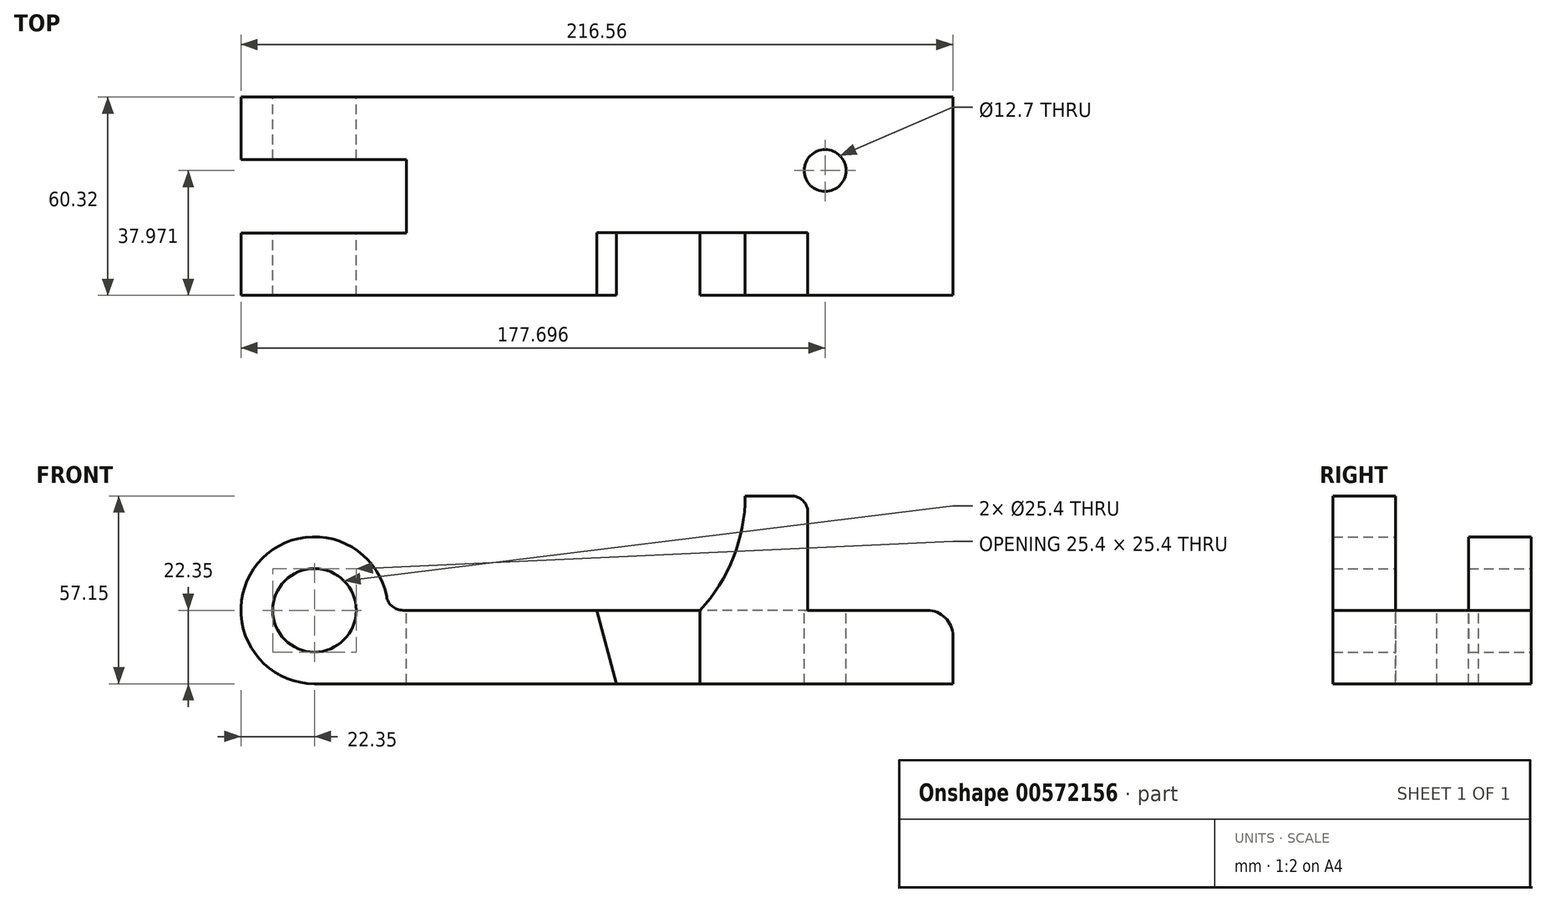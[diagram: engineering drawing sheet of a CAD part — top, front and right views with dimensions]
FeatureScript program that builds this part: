
annotation { "Feature Type Name" : "Feature", "Feature Type Description" : "" }
export const myFeature = defineFeature(function(context is Context, id is Id, definition is map)
    precondition{}
    {
        {
            var Q0;
            Q0=qCreatedBy(makeId("Front.planeOp"),FACE);
            var sketch = newSketch(context, id + "F0", { "sketchPlane" : qUnion([Q0])});
            skCircle(sketch, "E0", {"center": v(0, 0) * mm, "radius": 12.7 * mm});
            skCircle(sketch, "E1", {"center": v(0, 0) * mm, "radius": 22.35 * mm});
            skLineSegment(sketch, "E2", {"start": v(0, -22.35) * mm, "end": v(194.2, -22.35) * mm});
            skLineSegment(sketch, "E3", {"start": v(194.2, -22.35) * mm, "end": v(194.2, 0) * mm});
            skLineSegment(sketch, "E4", {"start": v(194.2, 0) * mm, "end": v(22.35, 0) * mm});
            skSolve(sketch);
        }
        {
            var Q0;
            Q0=makeQuery(id+"F0.imprint","IMPRINT",FACE,{"disambiguationData":[TD([[makeQuery(id+"F0.imprint","IMPRINT",EDGE,{"derivedFrom":sQuery(id+"F0.wireOp",EDGE,"E0")}),-1.0]])]});
            var Q1;
            {var subQ0=sQuery(id+"F0.wireOp",EDGE,"E2");Q1=makeQuery(id+"F0.imprint","IMPRINT",FACE,{"disambiguationData":[TD([[makeQuery(id+"F0.imprint","IMPRINT",EDGE,{"derivedFrom":subQ0}),1.0]])]});}
            extrude(context, id + "F1", {"entities" : qUnion([Q0, Q1]), "depth" : 30.16 * mm, "offsetDistance" : 25.4 * mm});
        }
        {
            var Q0;
            Q0=makeQuery(id+"F1.opExtrude","SWEPT_BODY",BODY,{"disambiguationData":[OSD([sQuery(id+"F0.wireOp",EDGE,"E0"),sQuery(id+"F0.wireOp",EDGE,"E1"),sQuery(id+"F0.wireOp",EDGE,"E2"),sQuery(id+"F0.wireOp",EDGE,"E3"),sQuery(id+"F0.wireOp",EDGE,"E4")])]});
            var Q1;
            Q1=qCreatedBy(makeId("Front.planeOp"),FACE);
            mirror(context, id + "F2", {"operationType" : NewBodyOperationType.ADD, "entities" : qUnion([Q0]), "mirrorPlane" : qUnion([Q1])});
        }
        {
            var Q0;
            {var subQ0=makeQuery(id+"F1.opExtrude","SWEPT_FACE",FACE,{"disambiguationData":[OSD([sQuery(id+"F0.wireOp",EDGE,"E4")])]});Q0=makeQuery(id+"F2.boolean.opBoolean","MERGE",FACE,{"derivedFrom":[subQ0,makeQuery(id+"F2.opPattern","COPY",FACE,{"derivedFrom":subQ0,"instanceName":"1"})]});}
            var sketch = newSketch(context, id + "F3", { "sketchPlane" : qUnion([Q0])});
            skLineSegment(sketch, "E5.bottom", {"start": v(27.96, 11.16) * mm, "end": v(-27.96, 11.16) * mm});
            skLineSegment(sketch, "E5.top", {"start": v(27.96, -11.16) * mm, "end": v(-27.96, -11.16) * mm});
            skLineSegment(sketch, "E5.left", {"start": v(27.96, 11.16) * mm, "end": v(27.96, -11.16) * mm});
            skLineSegment(sketch, "E5.right", {"start": v(-27.96, 11.16) * mm, "end": v(-27.96, -11.16) * mm});
            skPoint(sketch, "E5.middle", {"position": v(0, 0) * mm});
            skSolve(sketch);
        }
        {
            var Q0;
            {var subQ0=sQuery(id+"F3.wireOp",EDGE,"E5.left");Q0=makeQuery(id+"F3.imprint","IMPRINT",FACE,{"disambiguationData":[TD([[makeQuery(id+"F3.imprint","IMPRINT",EDGE,{"derivedFrom":subQ0}),-1.0]])]});}
            var Q1;
            {var subQ0=sQuery(id+"F3.wireOp",EDGE,"E5.right");Q1=makeQuery(id+"F3.imprint","IMPRINT",FACE,{"disambiguationData":[TD([[makeQuery(id+"F3.imprint","IMPRINT",EDGE,{"derivedFrom":subQ0}),1.0]])]});}
            extrude(context, id + "F4", {"entities" : qUnion([Q0, Q1]), "operationType" : NewBodyOperationType.REMOVE, "oppositeDirection" : true, "depth" : 25.4 * mm, "offsetDistance" : 25.4 * mm});
        }
        {
            var Q0;
            {var subQ0=makeQuery(id+"F1.opExtrude","SWEPT_FACE",FACE,{"disambiguationData":[OSD([sQuery(id+"F0.wireOp",EDGE,"E4")])]});Q0=makeQuery(id+"F2.boolean.opBoolean","MERGE",FACE,{"derivedFrom":[subQ0,makeQuery(id+"F2.opPattern","COPY",FACE,{"derivedFrom":subQ0,"instanceName":"1"})]});}
            var sketch = newSketch(context, id + "F5", { "sketchPlane" : qUnion([Q0])});
            skLineSegment(sketch, "E6", {"start": v(27.96, -11.16) * mm, "end": v(27.96, 11.16) * mm});
            skLineSegment(sketch, "E7", {"start": v(27.96, 11.16) * mm, "end": v(-41.68, 11.16) * mm});
            skLineSegment(sketch, "E8", {"start": v(27.96, -11.16) * mm, "end": v(-49.29, -11.16) * mm});
            skLineSegment(sketch, "E9", {"start": v(-49.29, -11.16) * mm, "end": v(-41.68, 11.16) * mm});
            skSolve(sketch);
        }
        {
            var Q0;
            Q0 = qSketchRegion(id + "F5", true);
            extrude(context, id + "F6", {"entities" : qUnion([Q0]), "operationType" : NewBodyOperationType.REMOVE, "depth" : 25.4 * mm, "offsetDistance" : 25.4 * mm});
        }
        {
            var Q0;
            {var subQ0=makeQuery(id+"F1.opExtrude","SWEPT_FACE",FACE,{"disambiguationData":[OSD([sQuery(id+"F0.wireOp",EDGE,"E4")])]});Q0=makeQuery(id+"F2.boolean.opBoolean","MERGE",FACE,{"derivedFrom":[subQ0,makeQuery(id+"F2.opPattern","COPY",FACE,{"derivedFrom":subQ0,"instanceName":"1"})]});}
            var sketch = newSketch(context, id + "F7", { "sketchPlane" : qUnion([Q0])});
            skCircle(sketch, "E10", {"center": v(155.35, 7.81) * mm, "radius": 6.35 * mm});
            skSolve(sketch);
        }
        {
            var Q0;
            Q0=makeQuery(id+"F7.imprint","IMPRINT",FACE,{"disambiguationData":[TD([[makeQuery(id+"F7.imprint","IMPRINT",EDGE,{"derivedFrom":sQuery(id+"F7.wireOp",EDGE,"E10")}),1.0]])]});
            extrude(context, id + "F8", {"entities" : qUnion([Q0]), "operationType" : NewBodyOperationType.REMOVE, "oppositeDirection" : true, "depth" : 25.4 * mm, "offsetDistance" : 25.4 * mm});
        }
        {
            var Q0;
            {var subQ0=makeQuery(id+"F1.opExtrude","SWEPT_EDGE",EDGE,{"disambiguationData":[OSD([sQuery(id+"F0.wireOp",EDGE,"E3"),sQuery(id+"F0.wireOp",EDGE,"E4")])]});Q0=makeQuery(id+"F2.boolean.opBoolean","MERGE",EDGE,{"derivedFrom":[subQ0,makeQuery(id+"F2.opPattern","COPY",EDGE,{"derivedFrom":subQ0,"instanceName":"1"})]});}
            fillet(context, id + "F9", {"entities" : qUnion([Q0]), "radius" : 7.87 * mm, "tangentPropagation" : true, "allowEdgeOverflow" : false});
        }
        {
            var Q0;
            {var subQ0=sQuery(id+"F0.wireOp",EDGE,"E1");var subQ1=makeQuery(id+"F1.opExtrude","SWEPT_FACE",FACE,{"disambiguationData":[OSD([subQ0])]});var subQ2=makeQuery(id+"F2.opPattern","COPY",FACE,{"derivedFrom":subQ1,"instanceName":"1"});var subQ3=sQuery(id+"F0.wireOp",EDGE,"E4");var subQ4=makeQuery(id+"F1.opExtrude","SWEPT_FACE",FACE,{"disambiguationData":[OSD([subQ3])]});var subQ5=makeQuery(id+"F2.opPattern","COPY",FACE,{"derivedFrom":subQ4,"instanceName":"1"});var subQ6=sQuery(id+"F3.wireOp",EDGE,"E5.top");var subQ7=makeQuery(id+"F1.opExtrude","SWEPT_EDGE",EDGE,{"disambiguationData":[OSD([subQ0,subQ3])]});Q0=makeQuery(id+"F4.boolean.opBoolean","SPLIT",EDGE,{"disambiguationData":[topologyDisambiguationEdgeConnected([subQ1,subQ4,subQ2,subQ5]),TD([makeQuery(id+"F4.opExtrude","SWEPT_FACE",FACE,{"disambiguationData":[OSD([subQ6])]})])],"derivedFrom":makeQuery(id+"F2.boolean.opBoolean","MERGE",EDGE,{"derivedFrom":[subQ7,makeQuery(id+"F2.opPattern","COPY",EDGE,{"derivedFrom":subQ7,"instanceName":"1"})]})});}
            var Q1;
            {var subQ0=sQuery(id+"F0.wireOp",EDGE,"E1");var subQ1=makeQuery(id+"F1.opExtrude","SWEPT_FACE",FACE,{"disambiguationData":[OSD([subQ0])]});var subQ2=makeQuery(id+"F2.opPattern","COPY",FACE,{"derivedFrom":subQ1,"instanceName":"1"});var subQ3=sQuery(id+"F0.wireOp",EDGE,"E4");var subQ4=makeQuery(id+"F1.opExtrude","SWEPT_FACE",FACE,{"disambiguationData":[OSD([subQ3])]});var subQ5=makeQuery(id+"F2.opPattern","COPY",FACE,{"derivedFrom":subQ4,"instanceName":"1"});var subQ6=sQuery(id+"F3.wireOp",EDGE,"E5.bottom");var subQ7=makeQuery(id+"F1.opExtrude","SWEPT_EDGE",EDGE,{"disambiguationData":[OSD([subQ0,subQ3])]});Q1=makeQuery(id+"F4.boolean.opBoolean","SPLIT",EDGE,{"disambiguationData":[topologyDisambiguationEdgeConnected([subQ1,subQ4,subQ2,subQ5]),TD([makeQuery(id+"F4.opExtrude","SWEPT_FACE",FACE,{"disambiguationData":[OSD([subQ6])]})])],"derivedFrom":makeQuery(id+"F2.boolean.opBoolean","MERGE",EDGE,{"derivedFrom":[subQ7,makeQuery(id+"F2.opPattern","COPY",EDGE,{"derivedFrom":subQ7,"instanceName":"1"})]})});}
            fillet(context, id + "F10", {"entities" : qUnion([Q0, Q1]), "radius" : 5.08 * mm, "tangentPropagation" : true, "allowEdgeOverflow" : false});
        }
        {
            var Q0;
            Q0=makeQuery(id+"F1.opExtrude","CAP_FACE",FACE,{"disambiguationData":[OSD([sQuery(id+"F0.wireOp",EDGE,"E0"),sQuery(id+"F0.wireOp",EDGE,"E1"),sQuery(id+"F0.wireOp",EDGE,"E2"),sQuery(id+"F0.wireOp",EDGE,"E3"),sQuery(id+"F0.wireOp",EDGE,"E4")])],"isStart":false});
            var sketch = newSketch(context, id + "F11", { "sketchPlane" : qUnion([Q0])});
            skLineSegment(sketch, "E11", {"start": v(85.85, 0) * mm, "end": v(91.85, -22.35) * mm});
            skLineSegment(sketch, "E12", {"start": v(91.85, -22.35) * mm, "end": v(117.25, -22.35) * mm});
            skLineSegment(sketch, "E13", {"start": v(117.25, -22.35) * mm, "end": v(117.25, 0) * mm});
            skLineSegment(sketch, "E14", {"start": v(117.25, 0) * mm, "end": v(85.85, 0) * mm});
            skSolve(sketch);
        }
        {
            var Q0;
            Q0=makeQuery(id+"F11.imprint","IMPRINT",FACE,{"disambiguationData":[TD([[makeQuery(id+"F11.imprint","IMPRINT",EDGE,{"derivedFrom":sQuery(id+"F11.wireOp",EDGE,"E11")}),1.0]])]});
            extrude(context, id + "F12", {"entities" : qUnion([Q0]), "operationType" : NewBodyOperationType.REMOVE, "oppositeDirection" : true, "depth" : 19.05 * mm, "offsetDistance" : 25.4 * mm});
        }
        {
            var Q0;
            {var subQ0=sQuery(id+"F0.wireOp",EDGE,"E4");var subQ2=sQuery(id+"F0.wireOp",EDGE,"E2");var subQ4=sQuery(id+"F0.wireOp",EDGE,"E3");var subQ5=makeQuery(id+"F1.opExtrude","SWEPT_FACE",FACE,{"disambiguationData":[OSD([subQ4])]});Q0=makeQuery(id+"F12.boolean.opBoolean","SPLIT",FACE,{"disambiguationData":[TD([subQ5])],"derivedFrom":makeQuery(id+"F1.opExtrude","CAP_FACE",FACE,{"disambiguationData":[OSD([sQuery(id+"F0.wireOp",EDGE,"E0"),sQuery(id+"F0.wireOp",EDGE,"E1"),subQ2,subQ4,subQ0])],"isStart":false})});}
            var sketch = newSketch(context, id + "F13", { "sketchPlane" : qUnion([Q0])});
            skLineSegment(sketch, "E15", {"start": v(150.09, 0) * mm, "end": v(150.09, 34.8) * mm});
            skLineSegment(sketch, "E16", {"start": v(131.04, 0) * mm, "end": v(131.04, 34.8) * mm});
            skLineSegment(sketch, "E17", {"start": v(131.04, 34.8) * mm, "end": v(150.09, 34.8) * mm});
            skSolve(sketch);
        }
        {
            var Q0;
            Q0 = qSketchRegion(id + "F13", true);
            var Q1;
            {var subQ0=sQuery(id+"F13.wireOp",EDGE,"E15");Q1=makeQuery(id+"F13.imprint","IMPRINT",FACE,{"disambiguationData":[TD([[makeQuery(id+"F13.imprint","IMPRINT",EDGE,{"derivedFrom":subQ0}),1.0]])]});}
            extrude(context, id + "F14", {"entities" : qUnion([Q0, Q1]), "operationType" : NewBodyOperationType.ADD, "oppositeDirection" : true, "depth" : 19.05 * mm, "offsetDistance" : 25.4 * mm});
        }
        {
            var Q0;
            Q0=makeQuery(id+"F14.opExtrude","SWEPT_EDGE",EDGE,{"disambiguationData":[OSD([sQuery(id+"F0.wireOp",EDGE,"E4"),sQuery(id+"F13.wireOp",EDGE,"E15")])]});
            var Q1;
            Q1=makeQuery(id+"F14.opExtrude","SWEPT_EDGE",EDGE,{"disambiguationData":[OSD([sQuery(id+"F13.wireOp",EDGE,"E15"),sQuery(id+"F13.wireOp",EDGE,"E17")])]});
            fillet(context, id + "F15", {"entities" : qUnion([Q0, Q1]), "radius" : 5.08 * mm, "tangentPropagation" : true, "allowEdgeOverflow" : false});
        }
        {
            var Q0;
            {var subQ0=sQuery(id+"F0.wireOp",EDGE,"E4");var subQ2=sQuery(id+"F0.wireOp",EDGE,"E2");var subQ4=sQuery(id+"F0.wireOp",EDGE,"E3");var subQ5=makeQuery(id+"F1.opExtrude","SWEPT_FACE",FACE,{"disambiguationData":[OSD([subQ4])]});Q0=makeQuery(id+"F14.boolean.opBoolean","MERGE",FACE,{"derivedFrom":[makeQuery(id+"F12.boolean.opBoolean","SPLIT",FACE,{"disambiguationData":[TD([subQ5])],"derivedFrom":makeQuery(id+"F1.opExtrude","CAP_FACE",FACE,{"disambiguationData":[OSD([sQuery(id+"F0.wireOp",EDGE,"E0"),sQuery(id+"F0.wireOp",EDGE,"E1"),subQ2,subQ4,subQ0])],"isStart":false})}),makeQuery(id+"F14.opExtrude","CAP_FACE",FACE,{"disambiguationData":[OSD([subQ0,sQuery(id+"F13.wireOp",EDGE,"E15"),sQuery(id+"F13.wireOp",EDGE,"E16"),sQuery(id+"F13.wireOp",EDGE,"E17")])],"isStart":true})]});}
            var sketch = newSketch(context, id + "F16", { "sketchPlane" : qUnion([Q0])});
            skArc(sketch, "E18", {"start": v(117.25, 0) * mm, "mid": v(127.46, 16.08) * mm, "end": v(131.04, 34.8) * mm});
            skSolve(sketch);
        }
        {
            var Q0;
            Q0 = qSketchRegion(id + "F16", true);
            var Q1;
            Q1=makeQuery(id+"F16.imprint","IMPRINT",FACE,{"disambiguationData":[TD([[makeQuery(id+"F16.imprint","IMPRINT",EDGE,{"derivedFrom":sQuery(id+"F16.wireOp",EDGE,"E18")}),-1.0]])]});
            extrude(context, id + "F17", {"entities" : qUnion([Q0, Q1]), "operationType" : NewBodyOperationType.ADD, "oppositeDirection" : true, "depth" : 19.05 * mm, "offsetDistance" : 25.4 * mm});
        }
    });
